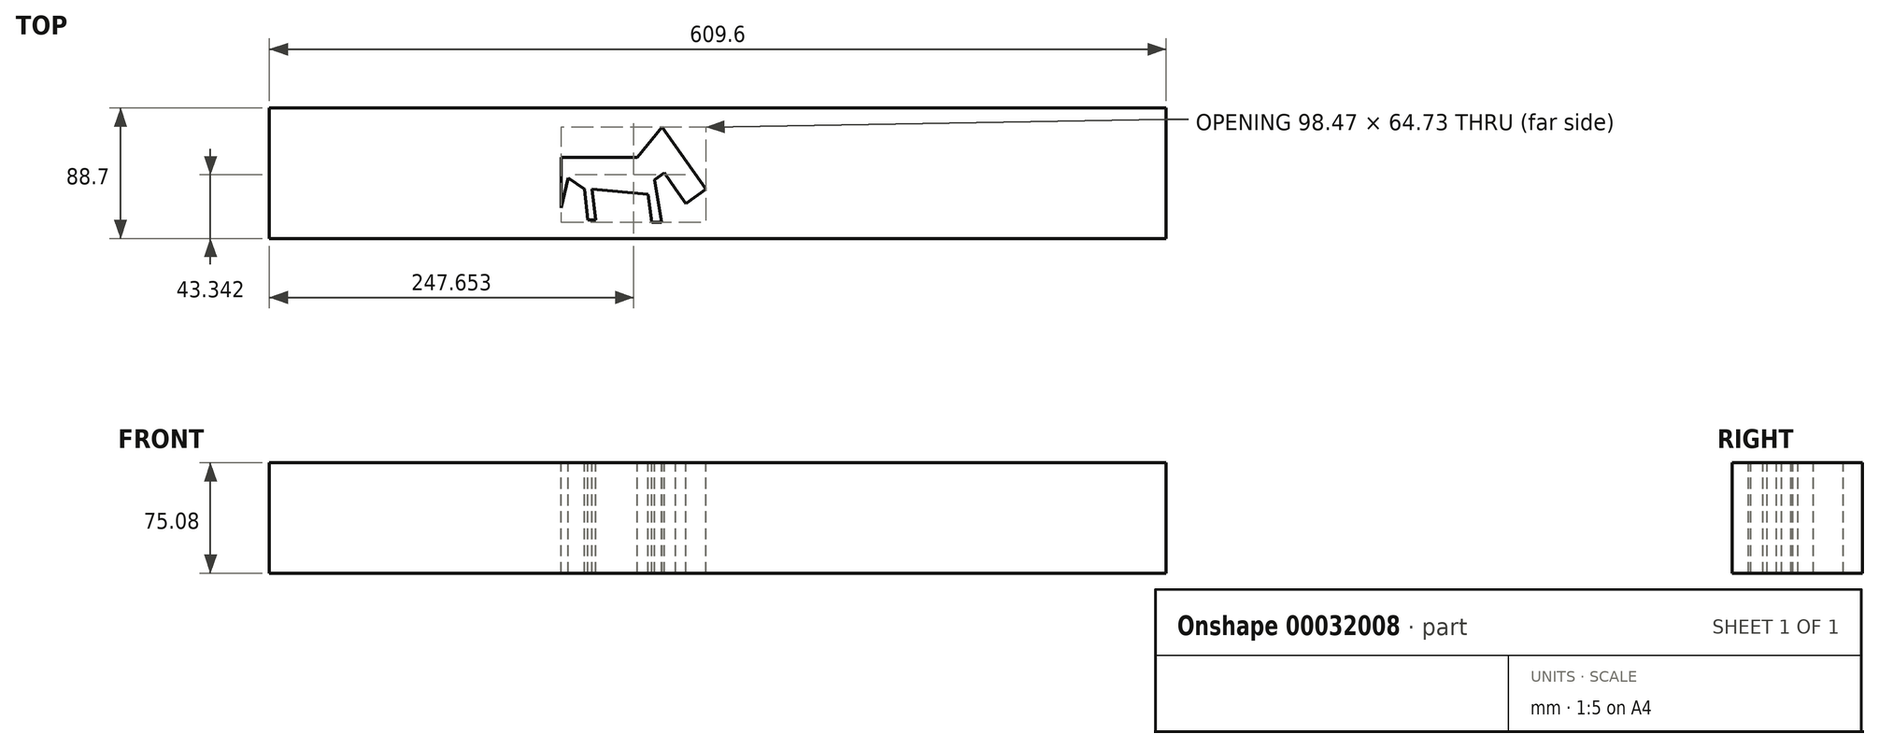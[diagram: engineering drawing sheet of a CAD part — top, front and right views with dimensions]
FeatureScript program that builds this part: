
annotation { "Feature Type Name" : "Feature", "Feature Type Description" : "" }
export const myFeature = defineFeature(function(context is Context, id is Id, definition is map)
    precondition{}
    {
        {
            var Q0;
            Q0=qCreatedBy(makeId("Right.planeOp"),FACE);
            var sketch = newSketch(context, id + "F0", { "sketchPlane" : qUnion([Q0])});
            skLineSegment(sketch, "E0.bottom", {"start": v(-33.51, 24.44) * mm, "end": v(55.2, 24.44) * mm});
            skLineSegment(sketch, "E0.top", {"start": v(-33.51, -50.64) * mm, "end": v(55.2, -50.64) * mm});
            skLineSegment(sketch, "E0.left", {"start": v(-33.51, 24.44) * mm, "end": v(-33.51, -50.64) * mm});
            skLineSegment(sketch, "E0.right", {"start": v(55.2, 24.44) * mm, "end": v(55.2, -50.64) * mm});
            skSolve(sketch);
        }
        {
            var Q0;
            Q0=makeQuery(id+"F0.imprint","IMPRINT",FACE,{"disambiguationData":[TD([[makeQuery(id+"F0.imprint","IMPRINT",EDGE,{"derivedFrom":sQuery(id+"F0.wireOp",EDGE,"E0.bottom")}),-1.0]])]});
            extrude(context, id + "F1", {"entities" : qUnion([Q0]), "depth" : 609.6 * mm});
        }
        {
            var Q0;
            Q0=makeQuery(id+"F1.opExtrude","SWEPT_FACE",FACE,{"disambiguationData":[OSD([sQuery(id+"F0.wireOp",EDGE,"E0.bottom")])]});
            var sketch = newSketch(context, id + "F2", { "sketchPlane" : qUnion([Q0])});
            skLineSegment(sketch, "E1", {"start": v(198.42, 21.74) * mm, "end": v(198.42, -12.58) * mm});
            skLineSegment(sketch, "E2", {"start": v(198.42, 21.74) * mm, "end": v(250.05, 21.74) * mm});
            skLineSegment(sketch, "E3", {"start": v(250.05, 21.74) * mm, "end": v(267, 42.2) * mm});
            skLineSegment(sketch, "E4", {"start": v(267, 42.2) * mm, "end": v(296.89, 0) * mm});
            skLineSegment(sketch, "E5", {"start": v(296.89, 0) * mm, "end": v(283.15, -9.73) * mm});
            skLineSegment(sketch, "E6", {"start": v(283.15, -9.73) * mm, "end": v(276.27, 0) * mm});
            skLineSegment(sketch, "E7", {"start": v(276.27, 0) * mm, "end": v(268.58, 11.15) * mm});
            skLineSegment(sketch, "E8", {"start": v(268.58, 11.15) * mm, "end": v(261.98, 6.6) * mm});
            skLineSegment(sketch, "E9", {"start": v(261.98, 6.6) * mm, "end": v(266.57, -22.53) * mm});
            skLineSegment(sketch, "E10", {"start": v(266.57, -22.53) * mm, "end": v(259.77, -22.53) * mm});
            skLineSegment(sketch, "E11", {"start": v(259.77, -22.53) * mm, "end": v(257.37, -3.46) * mm});
            skLineSegment(sketch, "E12", {"start": v(257.37, -3.46) * mm, "end": v(219.4, 0) * mm});
            skLineSegment(sketch, "E13", {"start": v(219.4, 0) * mm, "end": v(221.96, -20.74) * mm});
            skLineSegment(sketch, "E14", {"start": v(221.96, -20.74) * mm, "end": v(216.56, -20.74) * mm});
            skLineSegment(sketch, "E15", {"start": v(216.56, -20.74) * mm, "end": v(214.26, 0) * mm});
            skLineSegment(sketch, "E16", {"start": v(214.26, 0) * mm, "end": v(203.08, 7.65) * mm});
            skLineSegment(sketch, "E17", {"start": v(203.08, 7.65) * mm, "end": v(198.42, -12.58) * mm});
            skSolve(sketch);
        }
        {
            var Q0;
            Q0=makeQuery(id+"F2.imprint","IMPRINT",FACE,{"disambiguationData":[TD([[makeQuery(id+"F2.imprint","IMPRINT",EDGE,{"derivedFrom":sQuery(id+"F2.wireOp",EDGE,"E1")}),1.0]])]});
            extrude(context, id + "F3", {"entities" : qUnion([Q0]), "operationType" : NewBodyOperationType.REMOVE, "endBound" : BoundingType.THROUGH_ALL, "oppositeDirection" : true, "depth" : 25.4 * mm});
        }
    });
